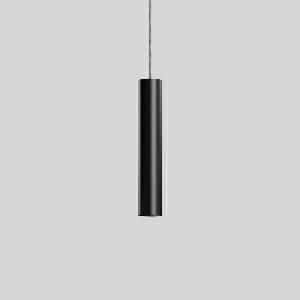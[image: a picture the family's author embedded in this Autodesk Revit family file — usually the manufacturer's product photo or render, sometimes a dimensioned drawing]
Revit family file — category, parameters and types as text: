
# Revit family: deecos_p_micro_911492_003_2_1b5c
name_source: partatom
category: Lighting Fixtures
units: mm (PartAtom-declared; Revit-internal decimal feet)

## family parameters
Cut with Voids When Loaded = No
Host = Face
Light Source = No
Part Type = Normal
Room Calculation Point = No
Round Connector Dimension = Use Diameter
Shared = No

## types (1)
- DEECOS P micro (1 x LED Modul 940, 1350 lm, 4000)
    Apparent Load = 16 VA
    CIE Flux Codes = 92 99 100 100 100
    Color Rendering = 92
    Color Temperature = 4000
    Default Elevation = 1800 mm
    Description = Series: DEECOS P micro
Cylindrical pendant luminaire. Housing: die-cast aluminium, powder-coated. Canopy made of powder-coated sheet steel with magnetic attachment. Optical assembly with lens made of plastic (polycarbonate) for the best homogeneous light distribution - can be changed without tools. Black plastic ring and recessed LED to prevent glare from the side. Best colour rendering index Ra>90. Transparent suspension cable 3 m, can be shortened. High quality converter without flickering and stroboscopic effect. 
Colour: deep black, matt (RAL 9005)
Diameter: 60 mm
Height: 340 mm
Suspension length: 3000 mm
Lamp: LED
Socket: without socket
Colour temperature: 4000K
Colour rendering index (CRI): 92
System power: 16 W
Rated luminous flux: 1350 lm
Luminous efficiency: 84 lm/W
Control gear: Regulated power supply
Protection class: I
Type of protection: IP 20
    Height = 340 mm
    Lamp = 1 x LED Modul 940
    Lamp Light Flux = 1350 lm
    Lamp count = 1
    Length = 60 mm  [stored 0.19685 ft]
    Lifetime = 50000 h
    Luminous efficacy = 84 lm/W
    Manufacturer = RZB
    ModVariant = No
    Model = 911492.003.2
    Mounting Place = Ceiling
    Mounting Type = Pendant
    Number of Poles = 1
    OnlyDefault = Yes
    Power Factor = 1
    Product Name = DEECOS P micro
    Product group = Pendant luminaires
    ProductGroupID = 902
    Protection Class = Protection class I
    Protection Degree = Degree of protection
    RLX_Detail_Level = 1
    RLX_Emergency_Light_Flux = 0 lm
    RLX_Emergency_Type = 0
    RLX_Emergency_Type_DB = No
    RlxData = <blob elided: 32149 chars, md5=c091293e>
    Socket = socket
    Standby Power = 0 W
    System Light Flux = 1350 lm
    System Power = 16 W
    Type Comments = Product without accessories
    Type Image = 911491.003.jpg
    URL = http://relux.com
    VarID = ---
    Voltage = 0 V
    Weight = 0.00 kg
    Width = 0 mm  [stored 0 ft]

note: [stored X ft] marks values corroborated as IEEE doubles in the binary element streams (Revit-internal decimal feet)

## geometry (parser evidence)
native form markers: Blend x4, Sweep x10
no freeform markers — native parametric forms only
